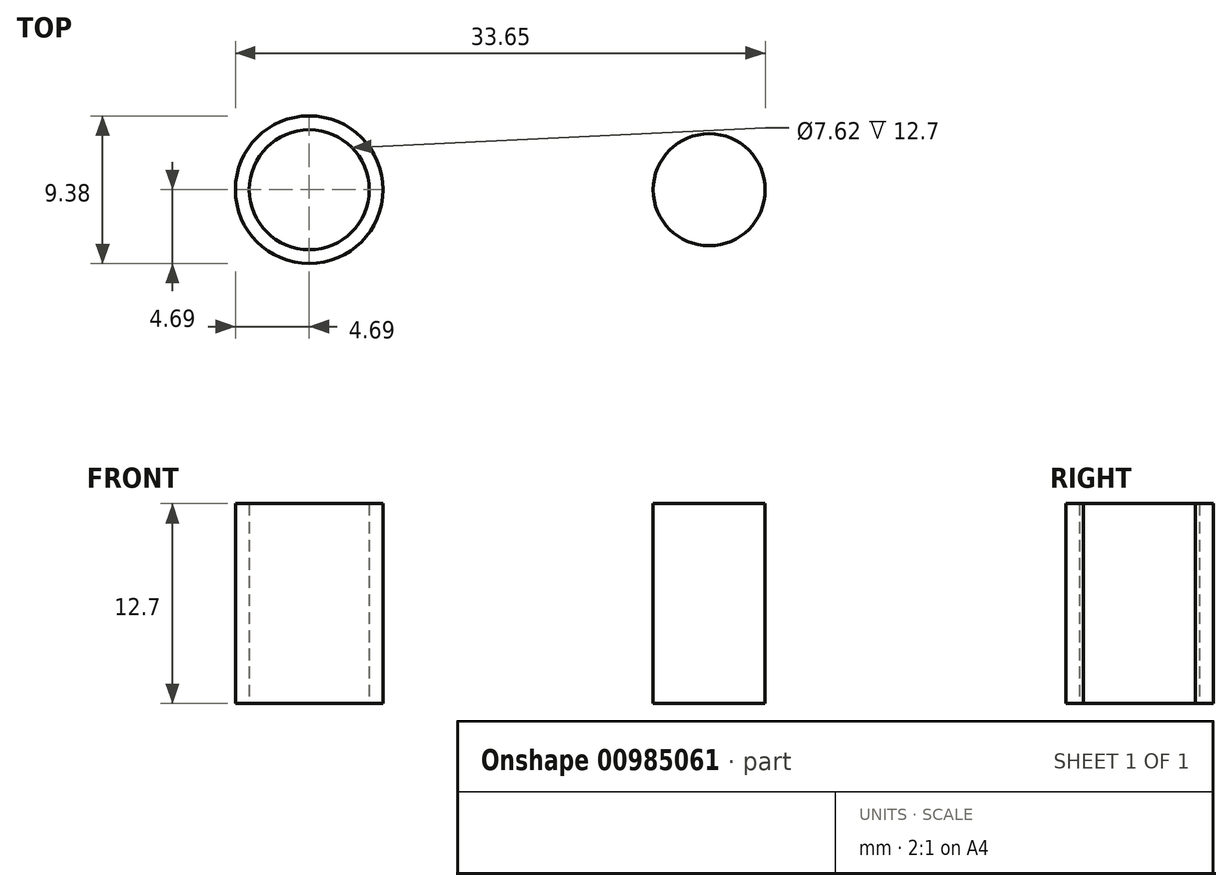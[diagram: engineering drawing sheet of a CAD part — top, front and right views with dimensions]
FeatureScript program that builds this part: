
annotation { "Feature Type Name" : "Feature", "Feature Type Description" : "" }
export const myFeature = defineFeature(function(context is Context, id is Id, definition is map)
    precondition{}
    {
        {
            var Q0;
            Q0=qCreatedBy(makeId("Top.planeOp"),FACE);
            var sketch = newSketch(context, id + "F0", { "sketchPlane" : qUnion([Q0])});
            skCircle(sketch, "E0", {"center": v(-25.4, 0) * mm, "radius": 3.81 * mm});
            skCircle(sketch, "E1", {"center": v(0, 0) * mm, "radius": 3.56 * mm});
            skCircle(sketch, "E2", {"center": v(-25.4, 0) * mm, "radius": 4.69 * mm});
            skSolve(sketch);
        }
        {
            var Q0;
            Q0=makeQuery(id+"F0.imprint","IMPRINT",FACE,{"disambiguationData":[TD([[makeQuery(id+"F0.imprint","IMPRINT",EDGE,{"derivedFrom":sQuery(id+"F0.wireOp",EDGE,"E0")}),-1.0]])]});
            var Q1;
            Q1=makeQuery(id+"F0.imprint","IMPRINT",FACE,{"disambiguationData":[TD([[makeQuery(id+"F0.imprint","IMPRINT",EDGE,{"derivedFrom":sQuery(id+"F0.wireOp",EDGE,"E1")}),1.0]])]});
            extrude(context, id + "F1", {"entities" : qUnion([Q0, Q1]), "depth" : 12.7 * mm, "offsetDistance" : 25.4 * mm});
        }
    });
